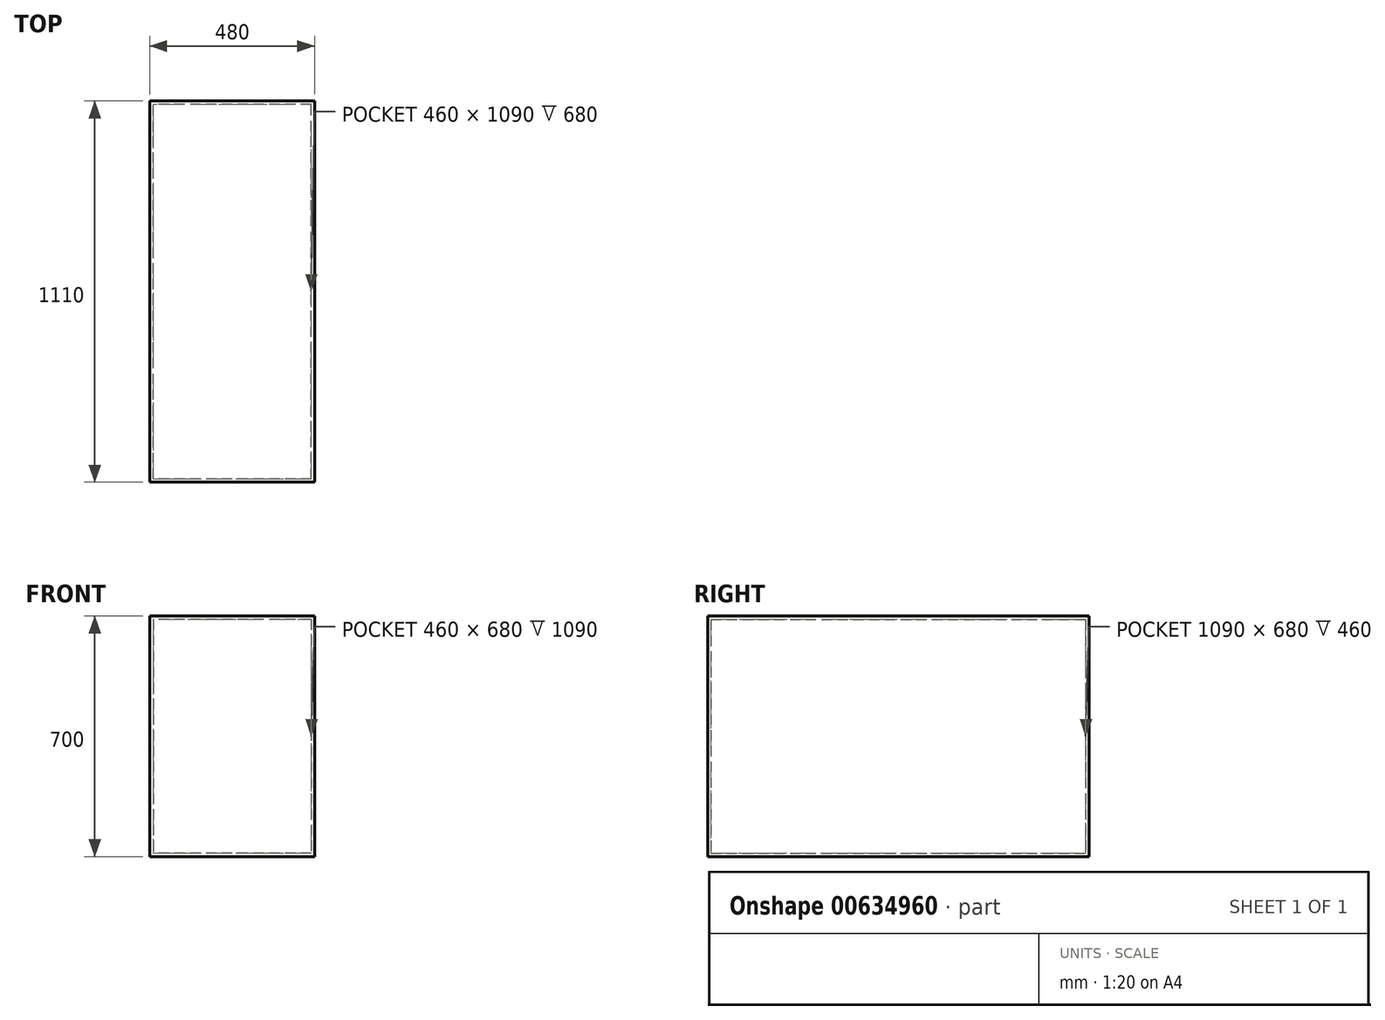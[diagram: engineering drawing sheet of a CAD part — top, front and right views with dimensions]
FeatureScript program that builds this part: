
annotation { "Feature Type Name" : "Feature", "Feature Type Description" : "" }
export const myFeature = defineFeature(function(context is Context, id is Id, definition is map)
    precondition{}
    {
        {
            var Q0;
            Q0=qCreatedBy(makeId("Top.planeOp"),FACE);
            var sketch = newSketch(context, id + "F0", { "sketchPlane" : qUnion([Q0])});
            skLineSegment(sketch, "E0.bottom", {"start": v(240, -555) * mm, "end": v(-240, -555) * mm});
            skLineSegment(sketch, "E0.top", {"start": v(240, 555) * mm, "end": v(-240, 555) * mm});
            skLineSegment(sketch, "E0.left", {"start": v(240, -555) * mm, "end": v(240, 555) * mm});
            skLineSegment(sketch, "E0.right", {"start": v(-240, -555) * mm, "end": v(-240, 555) * mm});
            skPoint(sketch, "E0.middle", {"position": v(0, 0) * mm});
            skCircle(sketch, "E1", {"center": v(79.87, 813.5) * mm, "radius": 12.5 * mm});
            skCircle(sketch, "E2", {"center": v(-127.83, 813.5) * mm, "radius": 31.5 * mm});
            skSolve(sketch);
        }
        {
            var Q0;
            Q0=makeQuery(id+"F0.imprint","IMPRINT",FACE,{"disambiguationData":[TD([[makeQuery(id+"F0.imprint","IMPRINT",EDGE,{"derivedFrom":sQuery(id+"F0.wireOp",EDGE,"E0.bottom")}),-1.0]])]});
            extrude(context, id + "F1", {"entities" : qUnion([Q0]), "endBound" : BoundingType.SYMMETRIC, "depth" : 700 * mm, "offsetDistance" : 25 * mm});
        }
        {
            var Q0;
            Q0=makeQuery(id+"F1.opExtrude","CAP_FACE",FACE,{"disambiguationData":[OSD([sQuery(id+"F0.wireOp",EDGE,"E0.bottom"),sQuery(id+"F0.wireOp",EDGE,"E0.top"),sQuery(id+"F0.wireOp",EDGE,"E0.left"),sQuery(id+"F0.wireOp",EDGE,"E0.right")])],"isStart":false});
            var Q1;
            Q1=makeQuery(id+"F1.opExtrude","SWEPT_BODY",BODY,{"disambiguationData":[OSD([sQuery(id+"F0.wireOp",EDGE,"E0.bottom"),sQuery(id+"F0.wireOp",EDGE,"E0.top"),sQuery(id+"F0.wireOp",EDGE,"E0.left"),sQuery(id+"F0.wireOp",EDGE,"E0.right")])]});
            shell(context, id + "F2", {"isHollow" : true, "entities" : qUnion([Q0]), "parts" : qUnion([Q1]), "thickness" : 10 * mm});
        }
        {
            var Q0;
            Q0=makeQuery(id+"F0.imprint","IMPRINT",FACE,{"disambiguationData":[TD([[makeQuery(id+"F0.imprint","IMPRINT",EDGE,{"derivedFrom":sQuery(id+"F0.wireOp",EDGE,"E2")}),1.0]])]});
            var Q1;
            Q1=makeQuery(id+"F0.imprint","IMPRINT",FACE,{"disambiguationData":[TD([[makeQuery(id+"F0.imprint","IMPRINT",EDGE,{"derivedFrom":sQuery(id+"F0.wireOp",EDGE,"E1")}),1.0]])]});
            var Q2;
            Q2=sQuery(id+"F0.wireOp",EDGE,"E2");
            var Q3;
            Q3=sQuery(id+"F0.wireOp",EDGE,"E1");
            extrude(context, id + "F3", {"entities" : qUnion([Q0, Q1]), "bodyType" : ToolBodyType.SURFACE, "surfaceEntities" : qUnion([Q2, Q3]), "depth" : (1650 - 350) * mm, "offsetDistance" : 25 * mm});
        }
    });
